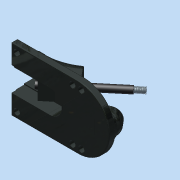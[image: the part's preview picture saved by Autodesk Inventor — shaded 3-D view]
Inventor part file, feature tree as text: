
AUTODESK INVENTOR PART (.ipt)
format: ipt  version: 2015 (Build 190159000, 159)  size: 1,542,144 bytes
history: native  units: in
note: dims shown in document units (in); Inventor stores cm internally (conversion verified against a paired STEP export)
features: other x7, plane x7, imported_body x6, sketch x1
ambient origin geometry x8: Origin, YZ Plane, XZ Plane, XY Plane, X Axis, Y Axis, Z Axis, Center Point
bodies: Body1 (feature_tree), Body2 (feature_tree), Body3 (feature_tree), Body4 (feature_tree), Body5 (feature_tree), Body6 (feature_tree)
feature tree (21):
  other  "Baseplate"
  other  "Baseplate.ipt1"
  plane  "Work Plane1"
  plane  "Work Plane2"
  plane  "Work Plane3"
  plane  "Work Plane4"
  plane  "Work Plane5"
  plane  "Work Plane6"
  plane  "Work Plane7"
  sketch  "3D Sketch1"
  other  "Baseplate_1"
  other  "Baseplate_2"
  other  "Baseplate_3"
  other  "Baseplate_4"
  other  "Baseplate_5"
  imported_body  "Base1"
  imported_body  "Base2"
  imported_body  "Base3"
  imported_body  "Base4"
  imported_body  "Base5"
  imported_body  "Base6"
